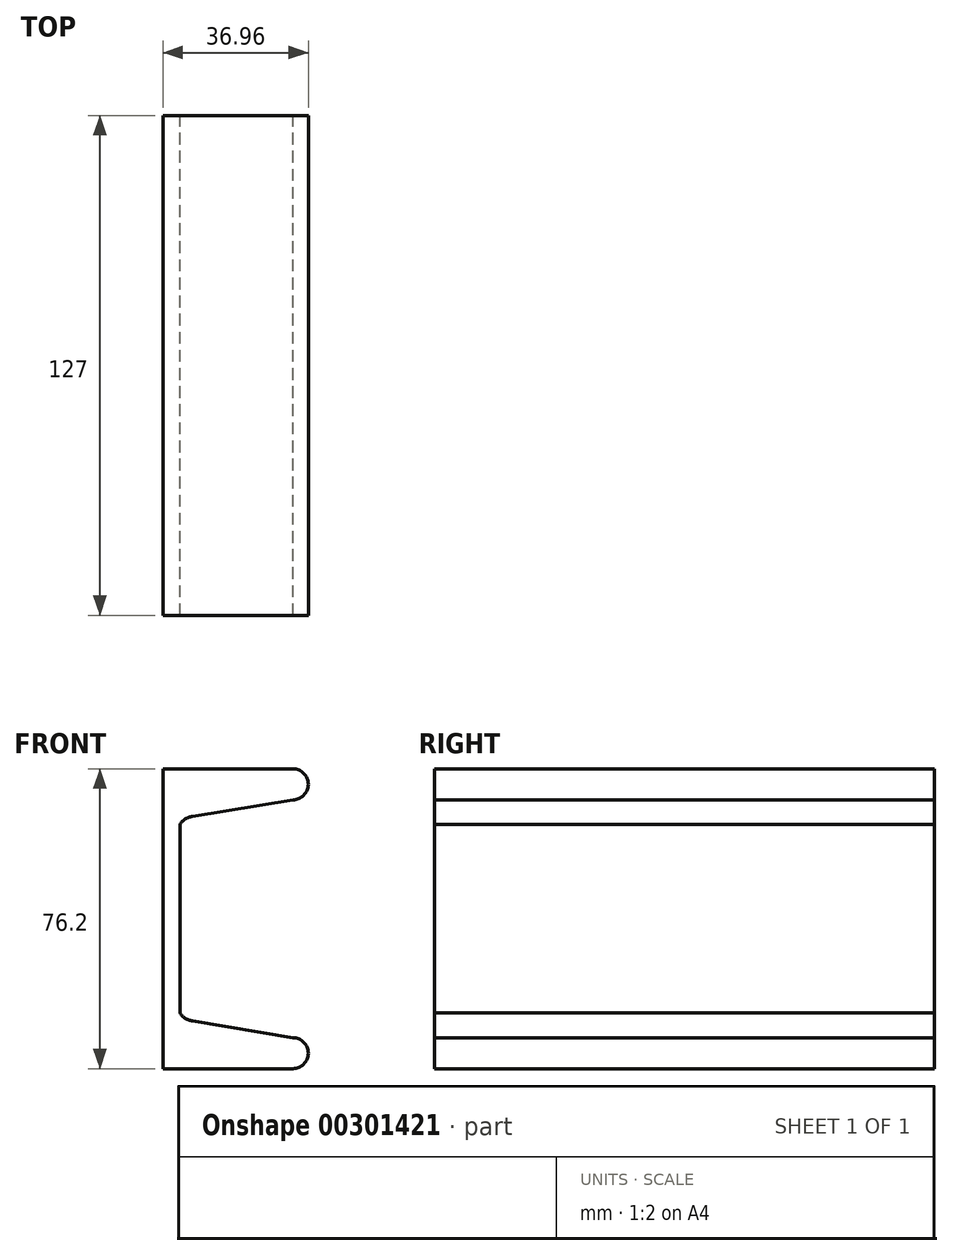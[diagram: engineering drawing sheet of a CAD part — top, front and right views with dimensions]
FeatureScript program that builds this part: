
annotation { "Feature Type Name" : "Feature", "Feature Type Description" : "" }
export const myFeature = defineFeature(function(context is Context, id is Id, definition is map)
    precondition{}
    {
        {
            var Q0;
            Q0=qCreatedBy(makeId("Front.planeOp"),FACE);
            var sketch = newSketch(context, id + "F0", { "sketchPlane" : qUnion([Q0])});
            skLineSegment(sketch, "E0", {"start": v(0, 0) * mm, "end": v(0, 38.1) * mm});
            skLineSegment(sketch, "E1", {"start": v(0, 38.1) * mm, "end": v(33.02, 38.1) * mm});
            skArc(sketch, "E2", {"start": v(33.02, 30.22) * mm, "mid": v(36.96, 34.16) * mm, "end": v(33.02, 38.1) * mm});
            skLineSegment(sketch, "E3", {"start": v(33.02, 30.22) * mm, "end": v(7.5, 25.98) * mm});
            skArc(sketch, "E4", {"start": v(7.5, 25.98) * mm, "mid": v(5.7, 25.3) * mm, "end": v(4.32, 23.98) * mm});
            skLineSegment(sketch, "E5", {"start": v(4.32, 23.98) * mm, "end": v(4.32, 0) * mm});
            skArc(sketch, "E6.MirrorCS", {"start": v(7.5, -25.98) * mm, "mid": v(5.7, -25.3) * mm, "end": v(4.32, -23.98) * mm});
            skArc(sketch, "E7.MirrorCS", {"start": v(33.02, -30.22) * mm, "mid": v(36.96, -34.16) * mm, "end": v(33.02, -38.1) * mm});
            skLineSegment(sketch, "E8.MirrorCS", {"start": v(33.02, -30.22) * mm, "end": v(7.5, -25.98) * mm});
            skLineSegment(sketch, "E9.MirrorCS", {"start": v(4.32, -23.98) * mm, "end": v(4.32, 0) * mm});
            skLineSegment(sketch, "E10.MirrorCS", {"start": v(0, 0) * mm, "end": v(0, -38.1) * mm});
            skLineSegment(sketch, "E11.MirrorCS", {"start": v(0, -38.1) * mm, "end": v(33.02, -38.1) * mm});
            skSolve(sketch);
        }
        {
            var Q0;
            Q0 = qSketchRegion(id + "F0", true);
            extrude(context, id + "F1", {"entities" : qUnion([Q0]), "endBound" : BoundingType.SYMMETRIC, "depth" : 127 * mm});
        }
    });
